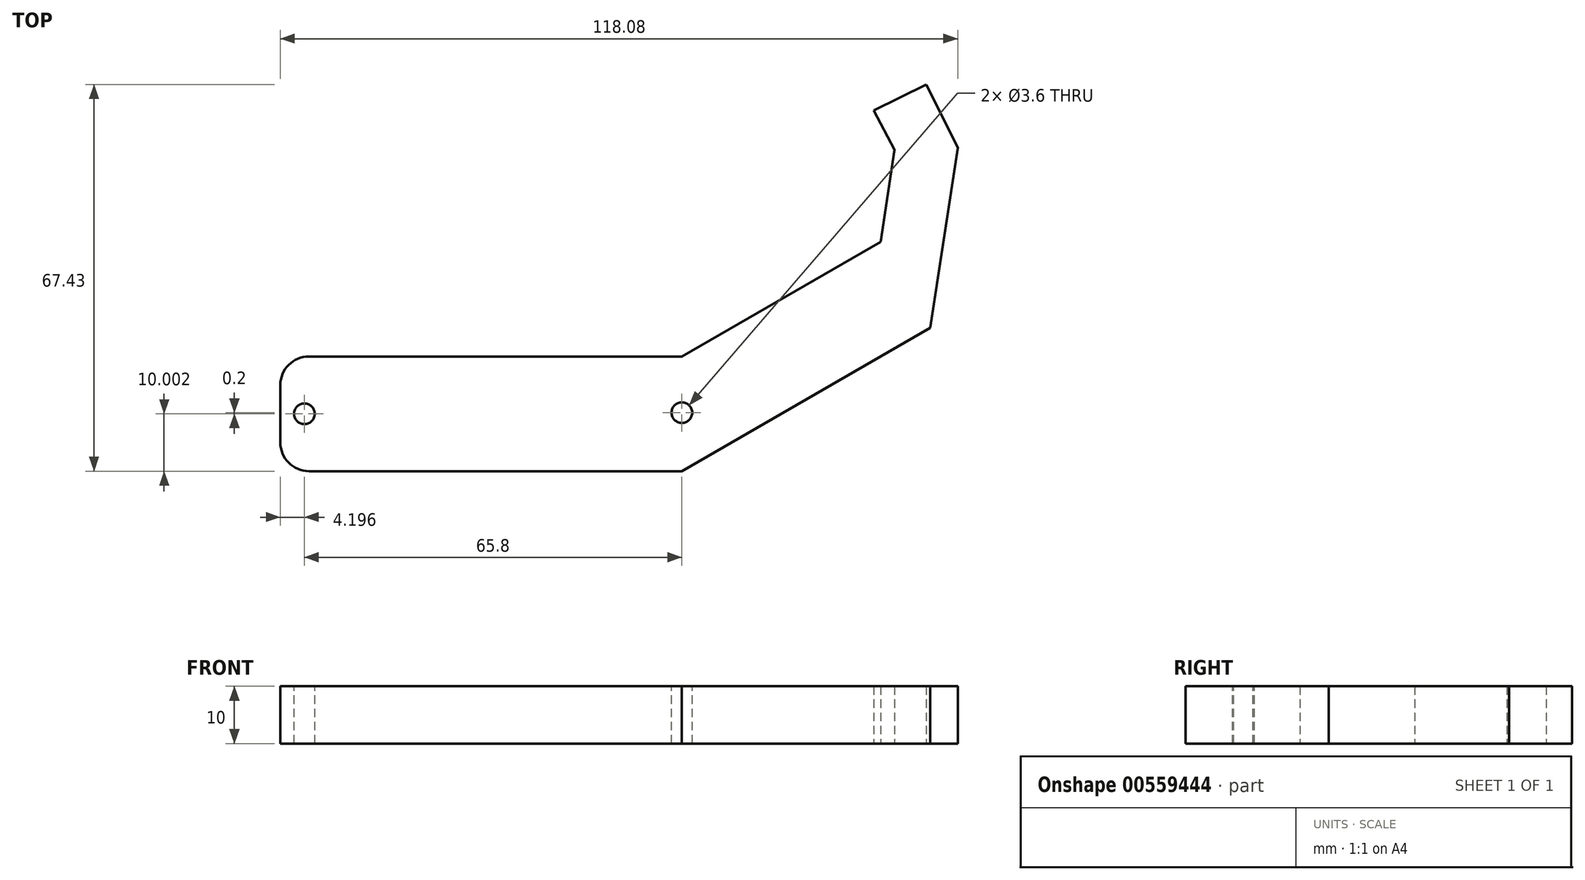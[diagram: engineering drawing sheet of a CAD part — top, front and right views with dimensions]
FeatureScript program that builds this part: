
annotation { "Feature Type Name" : "Feature", "Feature Type Description" : "" }
export const myFeature = defineFeature(function(context is Context, id is Id, definition is map)
    precondition{}
    {
        {
            var Q0;
            Q0=qCreatedBy(makeId("Top.planeOp"),FACE);
            var sketch = newSketch(context, id + "F0", { "sketchPlane" : qUnion([Q0])});
            skLineSegment(sketch, "E0.bottom", {"start": v(-10.9, -3.93) * mm, "end": v(-80.9, -3.93) * mm});
            skLineSegment(sketch, "E0.top", {"start": v(-10.9, 16.07) * mm, "end": v(-80.9, 16.07) * mm});
            skLineSegment(sketch, "E0.left", {"start": v(-10.9, -3.93) * mm, "end": v(-10.9, 16.07) * mm});
            skLineSegment(sketch, "E0.right", {"start": v(-80.9, -3.93) * mm, "end": v(-80.9, 16.07) * mm});
            skPoint(sketch, "E0.middle", {"position": v(-45.9, 6.07) * mm});
            skLineSegment(sketch, "E1", {"start": v(-10.9, 16.07) * mm, "end": v(23.75, 36.07) * mm});
            skLineSegment(sketch, "E2", {"start": v(-10.9, -3.93) * mm, "end": v(32.4, 21.07) * mm});
            skLineSegment(sketch, "E3", {"start": v(23.75, 36.07) * mm, "end": v(32.4, 21.07) * mm});
            skLineSegment(sketch, "E4", {"start": v(32.4, 21.07) * mm, "end": v(37.19, 52.47) * mm});
            skLineSegment(sketch, "E5", {"start": v(23.75, 36.07) * mm, "end": v(26.2, 52.14) * mm});
            skLineSegment(sketch, "E6", {"start": v(26.2, 52.14) * mm, "end": v(37.19, 52.47) * mm});
            skLineSegment(sketch, "E7", {"start": v(37.19, 52.47) * mm, "end": v(31.7, 63.5) * mm});
            skPoint(sketch, "E7.endSnap0", {"position": v(31.7, 52.3) * mm});
            skLineSegment(sketch, "E8", {"start": v(31.7, 63.5) * mm, "end": v(22.56, 58.95) * mm});
            skLineSegment(sketch, "E9", {"start": v(22.56, 58.95) * mm, "end": v(26.2, 52.14) * mm});
            skSolve(sketch);
        }
        {
            var Q0;
            Q0=qSketchRegion(id+"F0",true);
            extrude(context, id + "F1", {"entities" : qUnion([Q0]), "depth" : 10 * mm, "offsetDistance" : 25 * mm});
        }
        {
            var Q0;
            Q0=makeQuery(id+"F1.opExtrude","SWEPT_EDGE",EDGE,{"disambiguationData":[OSD([sQuery(id+"F0.wireOp",EDGE,"E0.top"),sQuery(id+"F0.wireOp",EDGE,"E0.right")])]});
            var Q1;
            Q1=makeQuery(id+"F1.opExtrude","SWEPT_EDGE",EDGE,{"disambiguationData":[OSD([sQuery(id+"F0.wireOp",EDGE,"E0.bottom"),sQuery(id+"F0.wireOp",EDGE,"E0.right")])]});
            fillet(context, id + "F2", {"entities" : qUnion([Q0, Q1]), "radius" : 5 * mm, "tangentPropagation" : true, "allowEdgeOverflow" : false});
        }
        {
            var Q0;
            Q0=makeQuery(id+"F1.opExtrude","CAP_FACE",FACE,{"disambiguationData":[OSD([sQuery(id+"F0.wireOp",EDGE,"E0.bottom"),sQuery(id+"F0.wireOp",EDGE,"E0.top"),sQuery(id+"F0.wireOp",EDGE,"E0.right"),sQuery(id+"F0.wireOp",EDGE,"E1"),sQuery(id+"F0.wireOp",EDGE,"E2"),sQuery(id+"F0.wireOp",EDGE,"E3")])],"isStart":false});
            var sketch = newSketch(context, id + "F3", { "sketchPlane" : qUnion([Q0])});
            skCircle(sketch, "E10", {"center": v(-76.7, 6.07) * mm, "radius": 1.8 * mm});
            skPoint(sketch, "E10.centerSnap0", {"position": v(-80.9, 6.07) * mm});
            skSolve(sketch);
        }
        {
            var Q0;
            Q0=qSketchRegion(id+"F3",true);
            extrude(context, id + "F4", {"entities" : qUnion([Q0]), "operationType" : NewBodyOperationType.REMOVE, "oppositeDirection" : true, "depth" : 20 * mm, "offsetDistance" : 25 * mm});
        }
        {
            var Q0;
            Q0=makeQuery(id+"F1.opExtrude","CAP_FACE",FACE,{"disambiguationData":[OSD([sQuery(id+"F0.wireOp",EDGE,"E0.bottom"),sQuery(id+"F0.wireOp",EDGE,"E0.top"),sQuery(id+"F0.wireOp",EDGE,"E0.right"),sQuery(id+"F0.wireOp",EDGE,"E1"),sQuery(id+"F0.wireOp",EDGE,"E2"),sQuery(id+"F0.wireOp",EDGE,"E3")])],"isStart":false});
            var sketch = newSketch(context, id + "F5", { "sketchPlane" : qUnion([Q0])});
            skCircle(sketch, "E11", {"center": v(-10.9, 6.27) * mm, "radius": 1.8 * mm});
            skSolve(sketch);
        }
        {
            var Q0;
            Q0=qSketchRegion(id+"F5",true);
            extrude(context, id + "F6", {"entities" : qUnion([Q0]), "operationType" : NewBodyOperationType.REMOVE, "oppositeDirection" : true, "depth" : 20 * mm, "offsetDistance" : 25 * mm});
        }
    });
